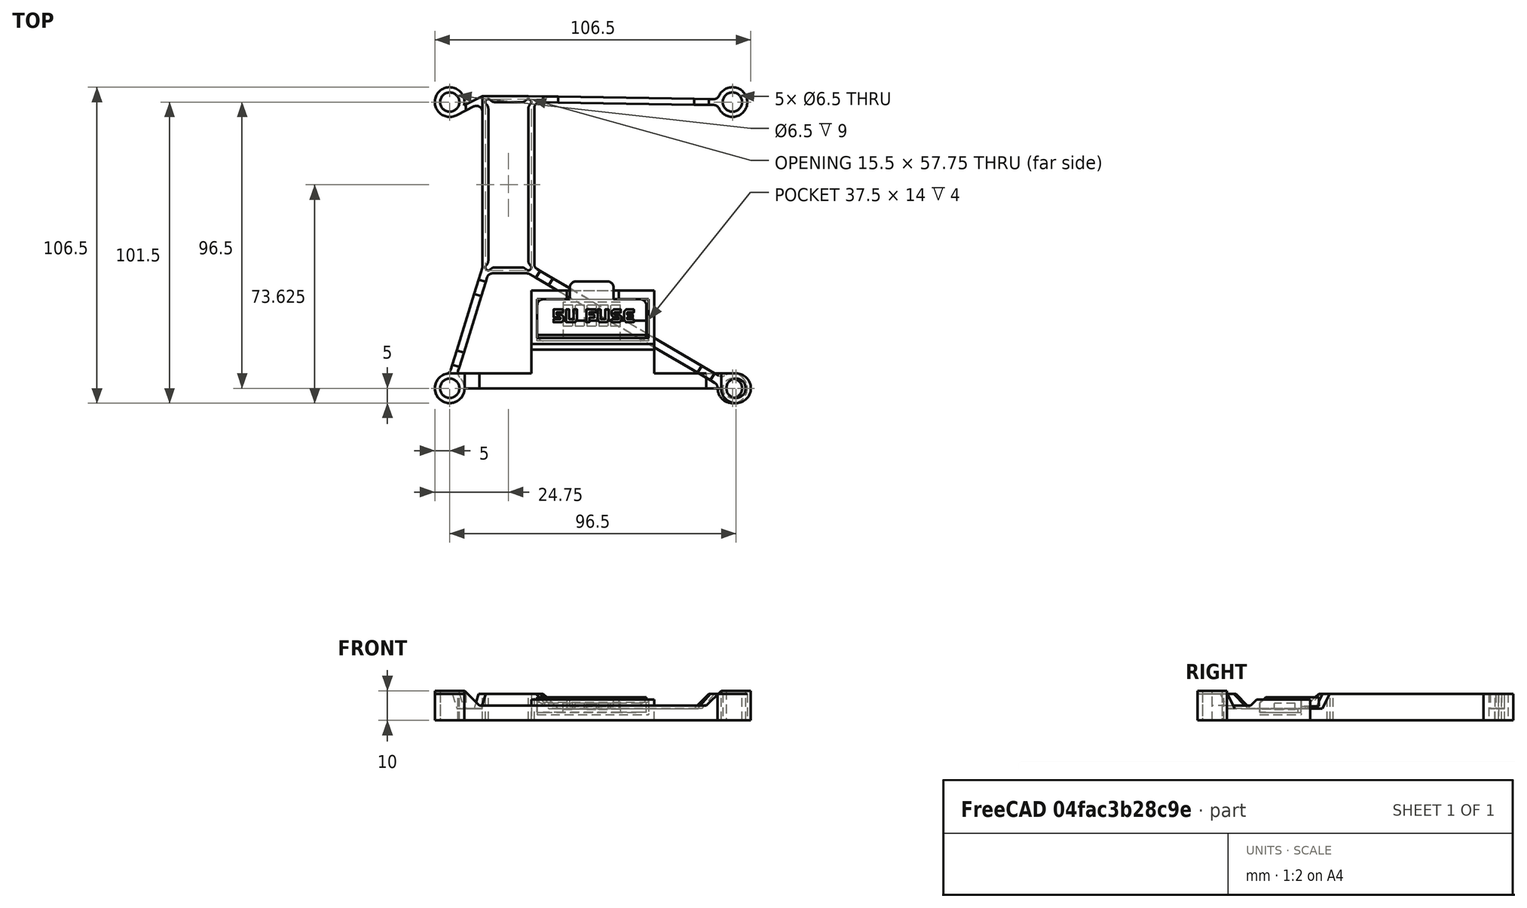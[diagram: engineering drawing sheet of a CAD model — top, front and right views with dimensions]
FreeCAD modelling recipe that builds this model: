
FCSTD DOCUMENT  (FreeCAD 0.17R13662 (Git))
Label: fuse_mount
License: CreativeCommons Attribution-ShareAlike
LicenseURL: http://creativecommons.org/licenses/by-sa/4.0/
objects: Sketcher::SketchObject×5, PartDesign::Pocket×4, App::FeaturePython×4, PartDesign::Pad×2, PartDesign::Chamfer×2, Part::FeaturePython×2, PartDesign::Body×1
note: 22 computed .brp shape members not serialized (recipe doc carries the construction recipe); baked Part::Feature solids carry a one-line shape summary decoded from their .brp

FEATURE [Sketcher::SketchObject] Sketch
  MapMode = 5
  Support = -> [XY_Plane]
  sketch-geometry (10):
    g0: Circle CenterX=0 CenterY=0 CenterZ=0 NormalX=0 NormalY=0 NormalZ=1 AngleXU=0 Radius=3.25
    g1: Circle CenterX=96.5 CenterY=0 CenterZ=0 NormalX=0 NormalY=0 NormalZ=1 AngleXU=0 Radius=3.25
    g2: LineSegment StartX=0 StartY=5 StartZ=0 EndX=27.5 EndY=5 EndZ=0
    g3: LineSegment StartX=27.5 StartY=5 StartZ=0 EndX=27.5 EndY=33 EndZ=0
    g4: LineSegment StartX=27.5 StartY=33 StartZ=0 EndX=69 EndY=33 EndZ=0
    g5: LineSegment StartX=5 StartY=0 StartZ=0 EndX=91.5 EndY=0 EndZ=0
    g6: ArcOfCircle CenterX=0 CenterY=0 CenterZ=0 NormalX=0 NormalY=0 NormalZ=1 AngleXU=0 Radius=5 StartAngle=1.5708 EndAngle=6.28319
    g7: ArcOfCircle CenterX=96.5 CenterY=0 CenterZ=0 NormalX=0 NormalY=0 NormalZ=1 AngleXU=0 Radius=5 StartAngle=3.14159 EndAngle=7.85398
    g8: LineSegment StartX=69 StartY=33 StartZ=0 EndX=69 EndY=5 EndZ=0
    g9: LineSegment StartX=69 StartY=5 StartZ=0 EndX=96.5 EndY=5 EndZ=0
  constraints (28):
    c: Coincident(g0,g-1)
    c: PointOnObject(g1,g-1)
    c: DistanceX(g1) = 96.5
    c: Radius(g1) = 3.25
    c: Equal(g1,g0)
    c: PointOnObject(g2,g-2)
    c: Horizontal(g2)
    c: Coincident(g2,g3)
    c: Vertical(g3)
    c: Coincident(g3,g4)
    c: Horizontal(g4)
    c: PointOnObject(g5,g-1)
    c: PointOnObject(g5,g-1)
    c: Coincident(g6,g-1)
    c: Coincident(g6,g2)
    c: Coincident(g6,g5)
    c: Coincident(g7,g1)
    c: Coincident(g7,g5)
    c: Radius(g7) = 5
    c: Equal(g7,g6)
    c: DistanceX(g4,g4) = 41.5
    c: DistanceY(g3,g3) = 28
    c: DistanceX(g2,g2) = 27.5
    c: Coincident(g4,g8)
    c: Vertical(g8)
    c: Coincident(g8,g9)
    c: Horizontal(g9)
    c: Tangent(g7,g9) = 1.5708
FEATURE [PartDesign::Pad] Pad
  Length = 10
  Length2 = 100
  Profile = -> Sketch
  Type = 0
FEATURE [Sketcher::SketchObject] Sketch001
  MapMode = 5
  Placement = pos=(0,0,10) rot=(0,0,1;0rad)
  Support = -> [Pad]
  sketch-geometry (8):
    g0: LineSegment StartX=10 StartY=5 StartZ=0 EndX=10 EndY=0 EndZ=0
    g1: LineSegment StartX=10 StartY=0 StartZ=0 EndX=86.5 EndY=0 EndZ=0
    g2: LineSegment StartX=86.5 StartY=5 StartZ=0 EndX=69 EndY=5 EndZ=0
    g3: LineSegment StartX=69 StartY=5 StartZ=0 EndX=69 EndY=13 EndZ=0
    g4: LineSegment StartX=69 StartY=13 StartZ=0 EndX=27.5 EndY=13 EndZ=0
    g5: LineSegment StartX=27.5 StartY=13 StartZ=0 EndX=27.5 EndY=5 EndZ=0
    g6: LineSegment StartX=27.5 StartY=5 StartZ=0 EndX=10 EndY=5 EndZ=0
    g7: LineSegment StartX=86.5 StartY=5 StartZ=0 EndX=86.5 EndY=0 EndZ=0
  constraints (24):
    c: PointOnObject(g0,g-1)
    c: Vertical(g0)
    c: Coincident(g0,g1)
    c: Horizontal(g1)
    c: Coincident(g2,g3)
    c: Vertical(g3)
    c: Coincident(g3,g4)
    c: Horizontal(g4)
    c: Coincident(g4,g5)
    c: Vertical(g5)
    c: Coincident(g5,g6)
    c: Coincident(g6,g0)
    c: Horizontal(g6)
    c: Horizontal(g2)
    c: DistanceY(g3,g3) = 8
    c: DistanceX(g4,g4) = 41.5
    c: DistanceY(g0,g0) = 5
    c: DistanceX(g0) = 10
    c: DistanceX(g6,g6) = 17.5
    c: Equal(g5,g3)
    c: Coincident(g2,g7)
    c: Coincident(g7,g1)
    c: Vertical(g7)
    c: Equal(g2,g6)
FEATURE [PartDesign::Pocket] Pocket
  BaseFeature = -> Pad
  Length = 5
  Length2 = 100
  Profile = -> Sketch001
  Type = 0
FEATURE [PartDesign::Pocket] Pocket001
  BaseFeature = -> Pocket
  Length = 3
  Length2 = 100
  Profile = -> Pocket [Face17]
  Type = 0
FEATURE [Sketcher::SketchObject] Sketch002
  MapMode = 5
  Placement = pos=(0,0,7) rot=(0,0,1;0rad)
  Support = -> [Pocket001]
  sketch-geometry (4):
    g0: LineSegment StartX=39.5 StartY=33 StartZ=0 EndX=57 EndY=33 EndZ=0
    g1: LineSegment StartX=57 StartY=33 StartZ=0 EndX=57 EndY=30 EndZ=0
    g2: LineSegment StartX=57 StartY=30 StartZ=0 EndX=39.5 EndY=30 EndZ=0
    g3: LineSegment StartX=39.5 StartY=30 StartZ=0 EndX=39.5 EndY=33 EndZ=0
  constraints (12):
    c: Coincident(g0,g1)
    c: Coincident(g1,g2)
    c: Coincident(g2,g3)
    c: Coincident(g3,g0)
    c: Horizontal(g0)
    c: Horizontal(g2)
    c: Vertical(g1)
    c: Vertical(g3)
    c: DistanceY(g1,g1) = 3
    c: DistanceX(g2) = 39.5
    c: DistanceY(g2) = 30
    c: DistanceX(g0,g0) = 17.5
FEATURE [PartDesign::Pocket] Pocket002
  BaseFeature = -> Pocket001
  Length = 3
  Length2 = 100
  Profile = -> Sketch002
  Type = 0
FEATURE [Sketcher::SketchObject] Sketch003
  MapMode = 5
  Placement = pos=(0,0,7) rot=(0,0,1;0rad)
  Support = -> [Pocket002]
  sketch-geometry (4):
    g0: LineSegment StartX=29.5 StartY=30 StartZ=0 EndX=67 EndY=30 EndZ=0
    g1: LineSegment StartX=67 StartY=30 StartZ=0 EndX=67 EndY=16 EndZ=0
    g2: LineSegment StartX=67 StartY=16 StartZ=0 EndX=29.5 EndY=16 EndZ=0
    g3: LineSegment StartX=29.5 StartY=16 StartZ=0 EndX=29.5 EndY=30 EndZ=0
  constraints (12):
    c: Coincident(g0,g1)
    c: Coincident(g1,g2)
    c: Coincident(g2,g3)
    c: Coincident(g3,g0)
    c: Horizontal(g0)
    c: Horizontal(g2)
    c: Vertical(g3)
    c: DistanceY(g1,g1) = 14
    c: DistanceY(g2) = 16
    c: DistanceX(g0,g0) = 37.5
    c: DistanceX(g0) = 29.5
    c: Vertical(g1)
FEATURE [PartDesign::Pocket] Pocket003
  BaseFeature = -> Pocket002
  Length = 5
  Length2 = 100
  Profile = -> Sketch003
  Type = 0
FEATURE [PartDesign::Chamfer] Chamfer
  Base = -> Pocket003 [Edge59]
  BaseFeature = -> Pocket003
  Size = 1.99
FEATURE [PartDesign::Chamfer] Chamfer001
  Base = -> Chamfer [Edge74,Edge75]
  BaseFeature = -> Chamfer
  Size = 4.99
FEATURE [Sketcher::SketchObject] Sketch004
  ExternalGeometry = -> [Chamfer001]
  MapMode = 5
  Placement = pos=(67,0,0) rot=(0.57735,-0.57735,-0.57735;2.0944rad)
  Support = -> [Chamfer001]
  sketch-geometry (3):
    g0: LineSegment StartX=-16 StartY=6 StartZ=0 EndX=-17 EndY=7 EndZ=0
    g1: LineSegment StartX=-17 StartY=7 StartZ=0 EndX=-16 EndY=7 EndZ=0
    g2: LineSegment StartX=-16 StartY=7 StartZ=0 EndX=-16 EndY=6 EndZ=0
  constraints (9):
    c: PointOnObject(g0,g-3)
    c: Coincident(g0,g1)
    c: Coincident(g1,g-3)
    c: Horizontal(g1)
    c: Coincident(g1,g2)
    c: Vertical(g2)
    c: Equal(g2,g1)
    c: DistanceX(g1,g1) = 1
    c: Coincident(g0,g2)
FEATURE [PartDesign::Pad] Pad001
  BaseFeature = -> Chamfer001
  Length = 37.5
  Length2 = 100
  Profile = -> Sketch004
  Type = 0
FEATURE [PartDesign::Body] Body
  Group = -> [Sketch,Pad,Sketch001,Sketch002,Sketch003,Pocket,Pocket001,Pocket002,Pocket003,Chamfer,Chamfer001,Sketch004,Pad001]
  Origin = -> Origin
  Tip = -> Pad001
FEATURE [Part::FeaturePython] heatsink_mount_v0_2_01  # a2plus imported part (geometry in sourceFile) (typed FeaturePython)
  fixedPosition = true
  sourceFile = <userpath>/Projects/taz-quiver/production_parts/printed_parts/heatsink_mount/heatsink_mount_v0.2.fcstd
  timeLastImport = 1.55352e+09
  updateColors = true
FEATURE [Part::FeaturePython] fuse_sleeve_01  # a2plus imported part (geometry in sourceFile) (typed FeaturePython)
  Placement = pos=(-32.5,2.25,2.75077) rot=(0,0,1;0rad)
  fixedPosition = false
  sourceFile = <userpath>/Projects/taz-redgum/production_parts/printed_parts/fuse_sleeve/fuse_sleeve.fcstd
  timeLastImport = 1.56106e+09
  updateColors = true
FEATURE [App::FeaturePython] planeConstraint01  label="planeConstraint01__fuse_sleeve_01"  # a2plus constraint (typed FeaturePython)
  Object1 = Pad001
  Object2 = fuse_sleeve_01
  SubElement1 = Face25
  SubElement2 = Face1
  Type = plane
  directionConstraint = 1
  offset = 0
FEATURE [App::FeaturePython] planeConstraint01_mirror  label="planeConstraint01__Pad001"  # a2plus constraint (typed FeaturePython)
  Object1 = Pad001
  Object2 = fuse_sleeve_01
  SubElement1 = Face25
  SubElement2 = Face1
  Type = plane
  directionConstraint = 1
  offset = 0
FEATURE [App::FeaturePython] planeConstraint02  label="planeConstraint02__fuse_sleeve_01"  # a2plus constraint (typed FeaturePython)
  Object1 = Pad001
  Object2 = fuse_sleeve_01
  SubElement1 = Face31
  SubElement2 = Face6
  Type = plane
  directionConstraint = 1
  offset = 0
FEATURE [App::FeaturePython] planeConstraint02_mirror  label="planeConstraint02__Pad001"  # a2plus constraint (typed FeaturePython)
  Object1 = Pad001
  Object2 = fuse_sleeve_01
  SubElement1 = Face31
  SubElement2 = Face6
  Type = plane
  directionConstraint = 1
  offset = 0
